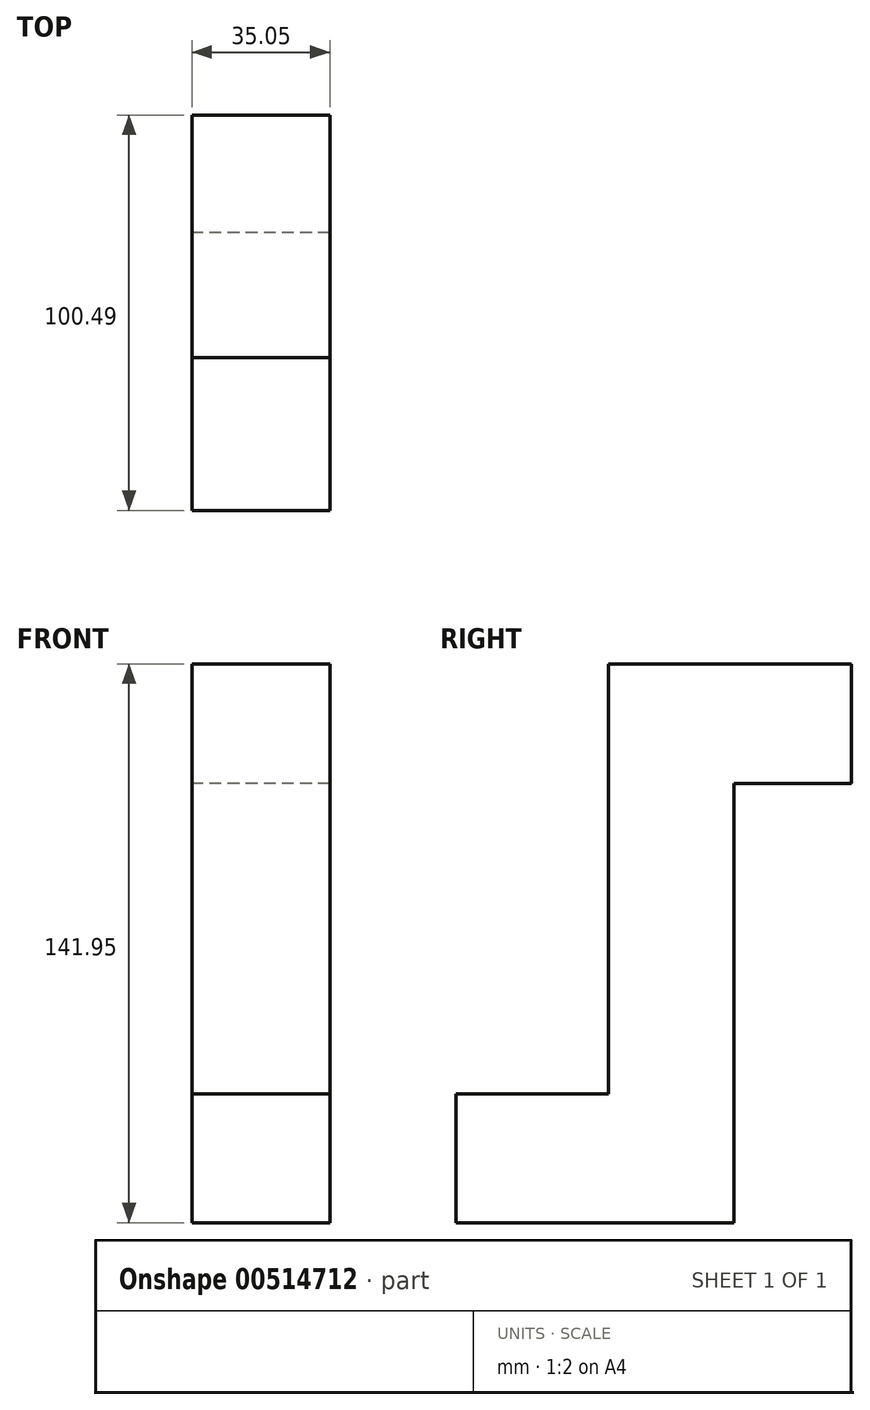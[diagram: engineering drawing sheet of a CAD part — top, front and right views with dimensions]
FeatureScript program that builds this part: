
annotation { "Feature Type Name" : "Feature", "Feature Type Description" : "" }
export const myFeature = defineFeature(function(context is Context, id is Id, definition is map)
    precondition{}
    {
        {
            var Q0;
            Q0=qCreatedBy(makeId("Right.planeOp"),FACE);
            var sketch = newSketch(context, id + "F0", { "sketchPlane" : qUnion([Q0])});
            skLineSegment(sketch, "E0.bottom", {"start": v(-49.64, 71.58) * mm, "end": v(50.85, 71.58) * mm});
            skLineSegment(sketch, "E0.top", {"start": v(-49.64, -70.37) * mm, "end": v(50.85, -70.37) * mm});
            skLineSegment(sketch, "E0.left", {"start": v(-49.64, 71.58) * mm, "end": v(-49.64, -70.37) * mm});
            skLineSegment(sketch, "E0.right", {"start": v(50.85, 71.58) * mm, "end": v(50.85, -70.37) * mm});
            skLineSegment(sketch, "E1", {"start": v(-49.64, -37.6) * mm, "end": v(-10.84, -37.6) * mm});
            skLineSegment(sketch, "E2", {"start": v(-10.84, -37.6) * mm, "end": v(-10.84, 71.58) * mm});
            skLineSegment(sketch, "E3", {"start": v(50.85, 41.2) * mm, "end": v(20.97, 41.2) * mm});
            skLineSegment(sketch, "E4", {"start": v(20.97, 41.2) * mm, "end": v(20.97, -41.2) * mm});
            skLineSegment(sketch, "E5", {"start": v(20.97, -41.2) * mm, "end": v(20.97, -64.83) * mm});
            skLineSegment(sketch, "E6", {"start": v(20.97, -64.83) * mm, "end": v(20.97, -70.37) * mm});
            skSolve(sketch);
        }
        {
            var Q0;
            {var subQ3=sQuery(id+"F0.wireOp",EDGE,"E1");Q0=makeQuery(id+"F0.imprint","IMPRINT",FACE,{"disambiguationData":[TD([[makeQuery(id+"F0.imprint","IMPRINT",EDGE,{"derivedFrom":subQ3}),-1.0]])]});}
            extrude(context, id + "F1", {"entities" : qUnion([Q0]), "depth" : 35.05 * mm, "offsetDistance" : 25.4 * mm});
        }
    });
